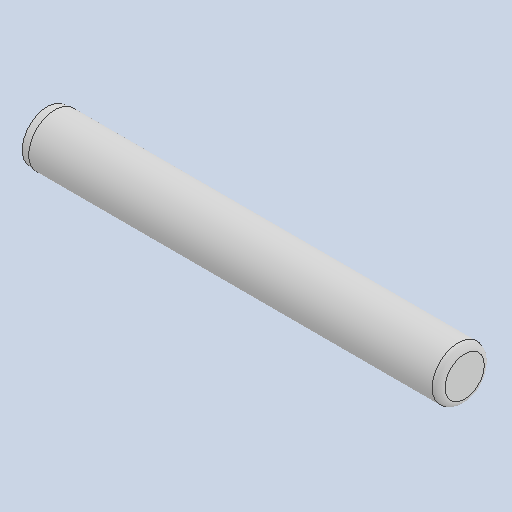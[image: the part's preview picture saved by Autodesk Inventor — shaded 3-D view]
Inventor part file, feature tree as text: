
AUTODESK INVENTOR PART (.ipt)
format: ipt  version: 2023 (Build 270158000, 158)  size: 97,792 bytes
history: native  units: in
note: dims shown in document units (in); Inventor stores cm internally (conversion verified against a paired STEP export)
features: revolve x1
ambient origin geometry x8: Origin, YZ Plane, XZ Plane, XY Plane, X Axis, Y Axis, Z Axis, Center Point
bodies: Solid1 (feature_tree)
feature tree (1):
  revolve  "Revolve1"  [1 undecoded]
note: 1 required parameter value undecoded (feature->parameter linkage not recoverable at this tier; creation-order binding heuristic only, values carry confidence <= 0.55)
